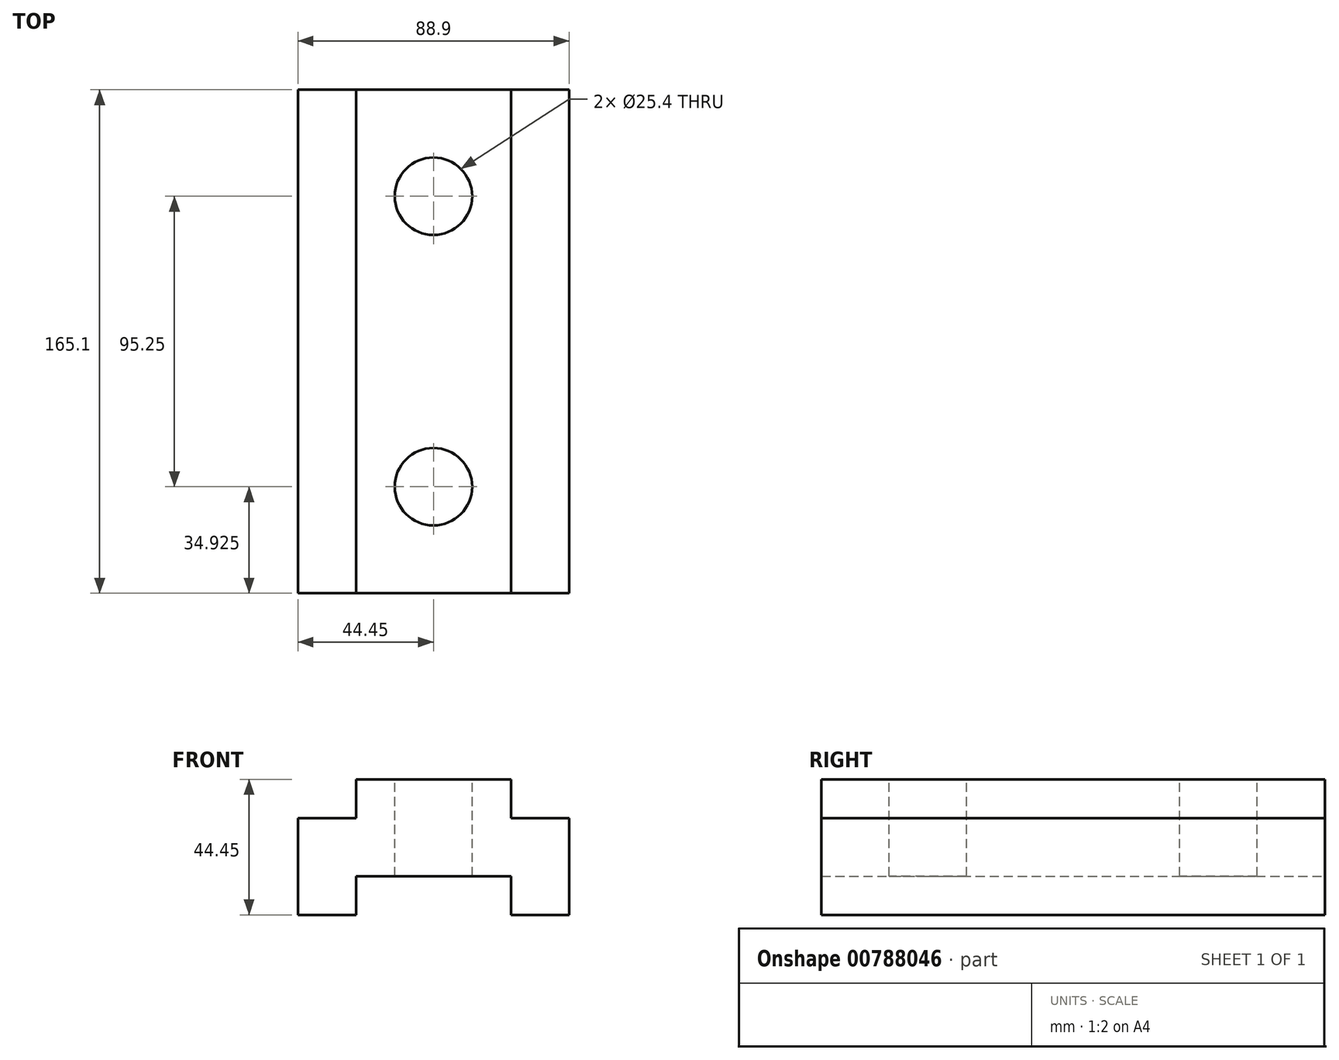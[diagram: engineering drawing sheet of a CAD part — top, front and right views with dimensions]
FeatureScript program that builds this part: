
annotation { "Feature Type Name" : "Feature", "Feature Type Description" : "" }
export const myFeature = defineFeature(function(context is Context, id is Id, definition is map)
    precondition{}
    {
        {
            var Q0;
            Q0=qCreatedBy(makeId("Front.planeOp"),FACE);
            var sketch = newSketch(context, id + "F0", { "sketchPlane" : qUnion([Q0])});
            skLineSegment(sketch, "E0", {"start": v(0, 0) * mm, "end": v(19.05, 0) * mm});
            skLineSegment(sketch, "E1", {"start": v(19.05, 0) * mm, "end": v(19.05, 12.7) * mm});
            skLineSegment(sketch, "E2", {"start": v(19.05, 12.7) * mm, "end": v(69.85, 12.7) * mm});
            skLineSegment(sketch, "E3", {"start": v(69.85, 12.7) * mm, "end": v(69.85, 0) * mm});
            skLineSegment(sketch, "E4", {"start": v(69.85, 0) * mm, "end": v(88.9, 0) * mm});
            skLineSegment(sketch, "E5", {"start": v(88.9, 0) * mm, "end": v(88.9, 31.75) * mm});
            skLineSegment(sketch, "E6", {"start": v(69.85, 31.75) * mm, "end": v(88.9, 31.75) * mm});
            skLineSegment(sketch, "E7", {"start": v(69.85, 44.45) * mm, "end": v(69.85, 31.75) * mm});
            skLineSegment(sketch, "E8", {"start": v(69.85, 44.45) * mm, "end": v(19.05, 44.45) * mm});
            skLineSegment(sketch, "E9", {"start": v(19.05, 44.45) * mm, "end": v(19.05, 31.75) * mm});
            skLineSegment(sketch, "E10", {"start": v(19.05, 31.75) * mm, "end": v(0, 31.75) * mm});
            skLineSegment(sketch, "E11", {"start": v(0, 31.75) * mm, "end": v(0, 0) * mm});
            skSolve(sketch);
        }
        {
            var Q0;
            Q0=makeQuery(id+"F0.imprint","IMPRINT",FACE,{"disambiguationData":[TD([[makeQuery(id+"F0.imprint","IMPRINT",EDGE,{"derivedFrom":sQuery(id+"F0.wireOp",EDGE,"E0")}),1.0]])]});
            extrude(context, id + "F1", {"entities" : qUnion([Q0]), "depth" : 165.1 * mm, "offsetDistance" : 25.4 * mm});
        }
        {
            var Q0;
            Q0=makeQuery(id+"F1.opExtrude","SWEPT_FACE",FACE,{"disambiguationData":[OSD([sQuery(id+"F0.wireOp",EDGE,"E8")])]});
            var sketch = newSketch(context, id + "F2", { "sketchPlane" : qUnion([Q0])});
            skLineSegment(sketch, "E12", {"start": v(44.45, 0) * mm, "end": v(44.45, -34.93) * mm, "construction": true});
            skLineSegment(sketch, "E13", {"start": v(44.45, -34.93) * mm, "end": v(44.45, -130.18) * mm, "construction": true});
            skCircle(sketch, "E14", {"center": v(44.45, -34.93) * mm, "radius": 12.7 * mm});
            skCircle(sketch, "E15", {"center": v(44.45, -130.18) * mm, "radius": 12.7 * mm});
            skSolve(sketch);
        }
        {
            var Q0;
            Q0 = qSketchRegion(id + "F2", true);
            extrude(context, id + "F3", {"entities" : qUnion([Q0]), "operationType" : NewBodyOperationType.REMOVE, "endBound" : BoundingType.UP_TO_NEXT, "oppositeDirection" : true, "depth" : 25.4 * mm, "offsetDistance" : 25.4 * mm});
        }
    });
